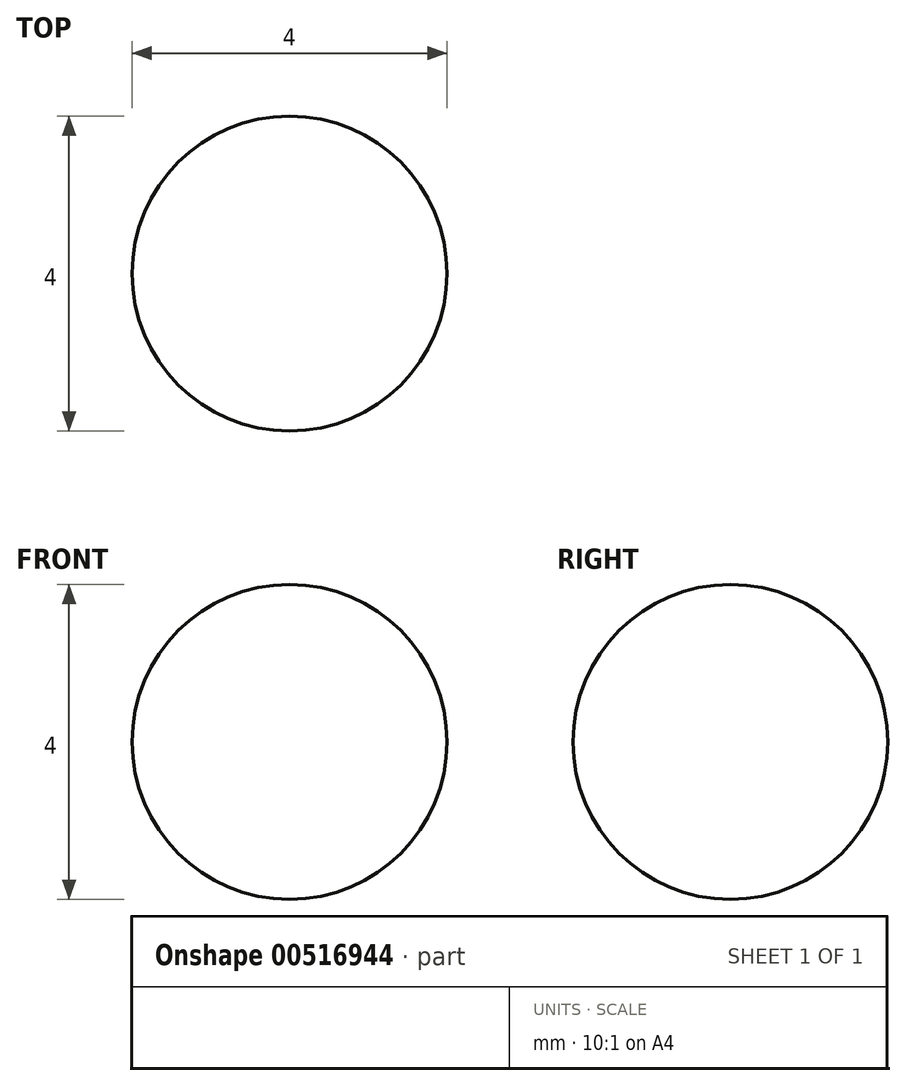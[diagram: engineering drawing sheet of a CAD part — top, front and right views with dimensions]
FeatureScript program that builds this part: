
annotation { "Feature Type Name" : "Feature", "Feature Type Description" : "" }
export const myFeature = defineFeature(function(context is Context, id is Id, definition is map)
    precondition{}
    {
        {
            var Q0;
            Q0=qCreatedBy(makeId("Front.planeOp"),FACE);
            var sketch = newSketch(context, id + "F0", { "sketchPlane" : qUnion([Q0])});
            skArc(sketch, "E0", {"start": v(0, 2) * mm, "mid": v(-2, 0) * mm, "end": v(0, -2) * mm});
            skLineSegment(sketch, "E1", {"start": v(0, 2) * mm, "end": v(0, -2) * mm});
            skSolve(sketch);
        }
        {
            var Q0;
            Q0=makeQuery(id+"F0.imprint","IMPRINT",FACE,{"disambiguationData":[TD([[makeQuery(id+"F0.imprint","IMPRINT",EDGE,{"derivedFrom":sQuery(id+"F0.wireOp",EDGE,"E0")}),1.0]])]});
            var Q1;
            Q1=sQuery(id+"F0.wireOp",EDGE,"E1");
            revolve(context, id + "F1", {"entities" : qUnion([Q0]), "axis" : qUnion([Q1]), "revolveType" : RevolveType.FULL});
        }
    });
